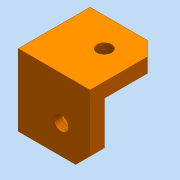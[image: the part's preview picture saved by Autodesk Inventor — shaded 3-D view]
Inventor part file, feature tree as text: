
AUTODESK INVENTOR PART (.ipt)
format: ipt  version: 2016 (Build 200138000, 138)  size: 155,136 bytes
history: native  units: mm
features: extrude x5, sketch x5, hole x3, chamfer x3
ambient origin geometry x8: Origin, YZ Plane, XZ Plane, XY Plane, X Axis, Y Axis, Z Axis, Center Point
bodies: Solid1 (feature_tree)
feature tree (16):
  extrude  "Extrusion1"  Depth=20.0mm
  extrude  "Extrusion2"  Depth=16.0mm TaperAngle=0.0deg
  hole  "Hole2"  [1 undecoded]
  hole  "Hole3"  [1 undecoded]
  hole  "Hole4"  [1 undecoded]
  chamfer  "Chamfer1"  Distance=7.0mm
  chamfer  "Chamfer2"  Distance=7.0mm
  chamfer  "Chamfer3"  Distance=7.0mm
  sketch  "Sketch3"  dims[d15=8.0mm d16=8.0mm d17=4.0mm d18=6.0mm d19=8.0mm d20=2.0mm d21=90.0deg d22=8.0mm d23=20.594885mm]
  sketch  "Sketch4"  dims[d24=8.0mm d25=8.0mm d26=4.0mm d27=6.0mm d28=8.0mm d29=2.0mm d30=90.0deg d31=8.0mm d32=20.594885mm]
  sketch  "Sketch5"  dims[d33=8.0mm d34=8.0mm d35=4.0mm d36=6.0mm d37=8.0mm d38=2.0mm d39=90.0deg d40=8.0mm d41=20.594885mm d42=4.0mm d43=2.0mm d44=45.0deg d45=4.0mm d46=2.0mm d47=45.0deg d48=4.0mm d49=2.0mm d50=45.0deg d51=7.0mm d52=7.0mm d53=7.0mm d54=2.0mm d55=0.0mm d56=2.0mm d57=0.0mm d58=2.0mm d59=0.0mm]
  extrude  "Extrusion3"  Depth=2.0mm TaperAngle=0.0deg
  extrude  "Extrusion4"  Depth=2.0mm TaperAngle=0.0deg
  extrude  "Extrusion5"  Depth=2.0mm TaperAngle=0.0deg
  sketch  "Sketch1"  dims[d0=20.0mm d1=20.0mm]
  sketch  "Sketch2"  dims[d2=4.0mm d3=0.0mm d4=16.0mm d5=0.0mm]
note: 3 required parameter values undecoded (feature->parameter linkage not recoverable at this tier; creation-order binding heuristic only, values carry confidence <= 0.55)
